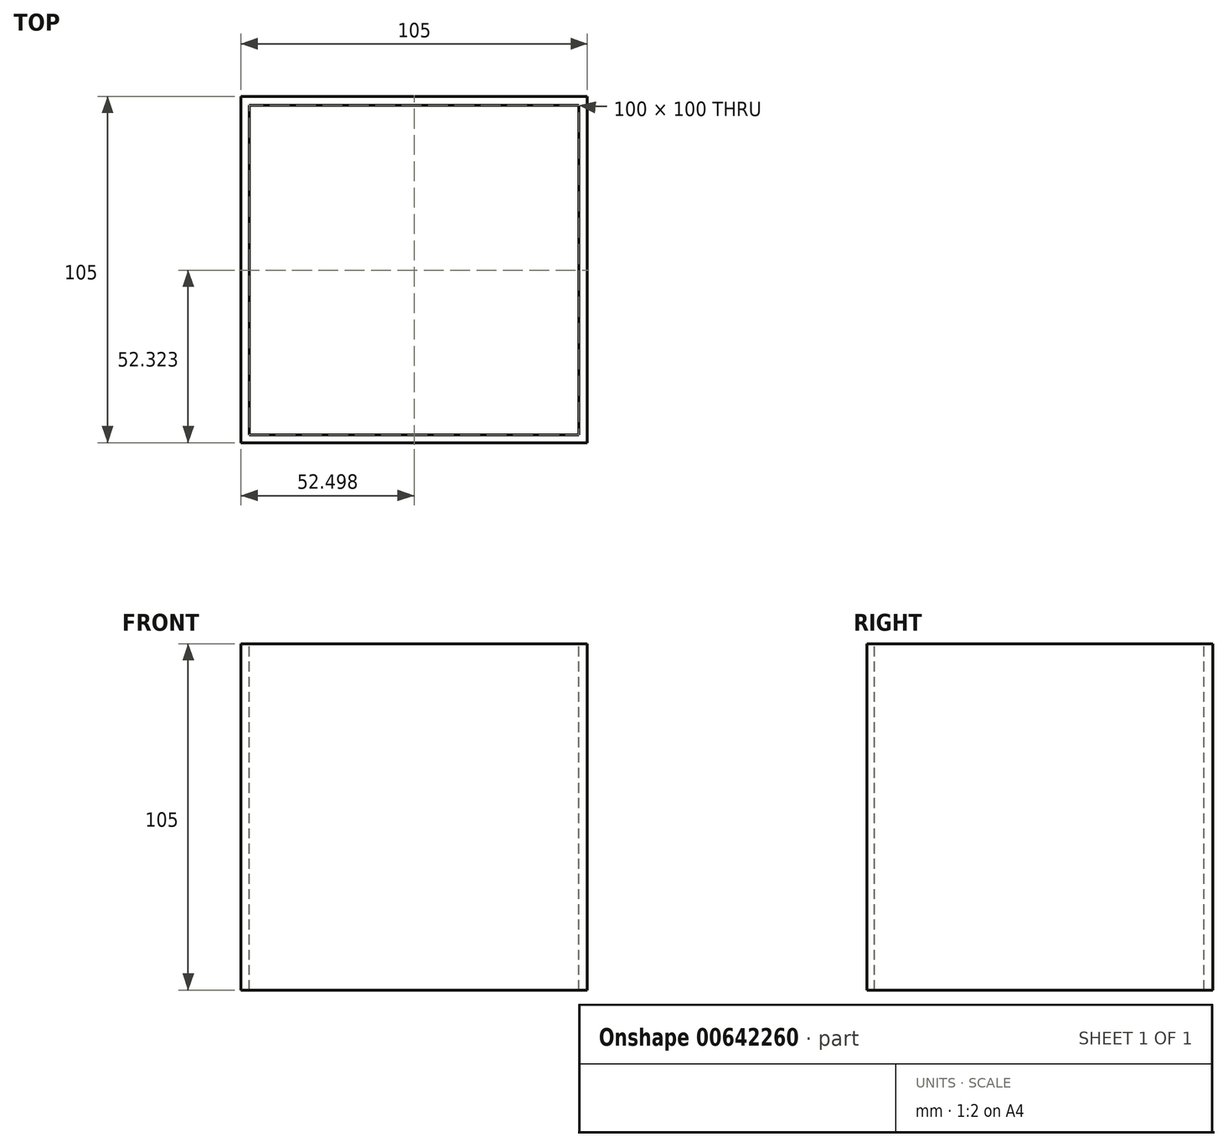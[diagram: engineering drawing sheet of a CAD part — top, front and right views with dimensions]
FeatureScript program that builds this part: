
annotation { "Feature Type Name" : "Feature", "Feature Type Description" : "" }
export const myFeature = defineFeature(function(context is Context, id is Id, definition is map)
    precondition{}
    {
        {
            var Q0;
            Q0=qCreatedBy(makeId("Top.planeOp"),FACE);
            var sketch = newSketch(context, id + "F0", { "sketchPlane" : qUnion([Q0])});
            skLineSegment(sketch, "E0.bottom", {"start": v(-47.45, 56.58) * mm, "end": v(57.55, 56.58) * mm});
            skLineSegment(sketch, "E0.top", {"start": v(-47.45, 161.58) * mm, "end": v(57.55, 161.58) * mm});
            skLineSegment(sketch, "E0.left", {"start": v(-47.45, 161.58) * mm, "end": v(-47.45, 56.58) * mm});
            skLineSegment(sketch, "E0.right", {"start": v(57.55, 161.58) * mm, "end": v(57.55, 56.58) * mm});
            skPoint(sketch, "E1.endSnap0", {"position": v(-47.45, 109.08) * mm});
            skLineSegment(sketch, "E2", {"start": v(-44.95, 109.08) * mm, "end": v(-44.95, 161.58) * mm});
            skLineSegment(sketch, "E3.bottom", {"start": v(-44.95, 158.9) * mm, "end": v(55.05, 158.9) * mm});
            skLineSegment(sketch, "E3.top", {"start": v(-44.95, 58.9) * mm, "end": v(55.05, 58.9) * mm});
            skLineSegment(sketch, "E3.left", {"start": v(-44.95, 158.9) * mm, "end": v(-44.95, 58.9) * mm});
            skLineSegment(sketch, "E3.right", {"start": v(55.05, 158.9) * mm, "end": v(55.05, 58.9) * mm});
            skSolve(sketch);
        }
        {
            var Q0;
            Q0=makeQuery(id+"F0.imprint","IMPRINT",FACE,{"disambiguationData":[TD([[makeQuery(id+"F0.imprint","IMPRINT",EDGE,{"derivedFrom":sQuery(id+"F0.wireOp",EDGE,"E0.bottom")}),1.0]])]});
            extrude(context, id + "F1", {"entities" : qUnion([Q0]), "depth" : -105 * mm, "offsetDistance" : 25 * mm});
        }
    });
